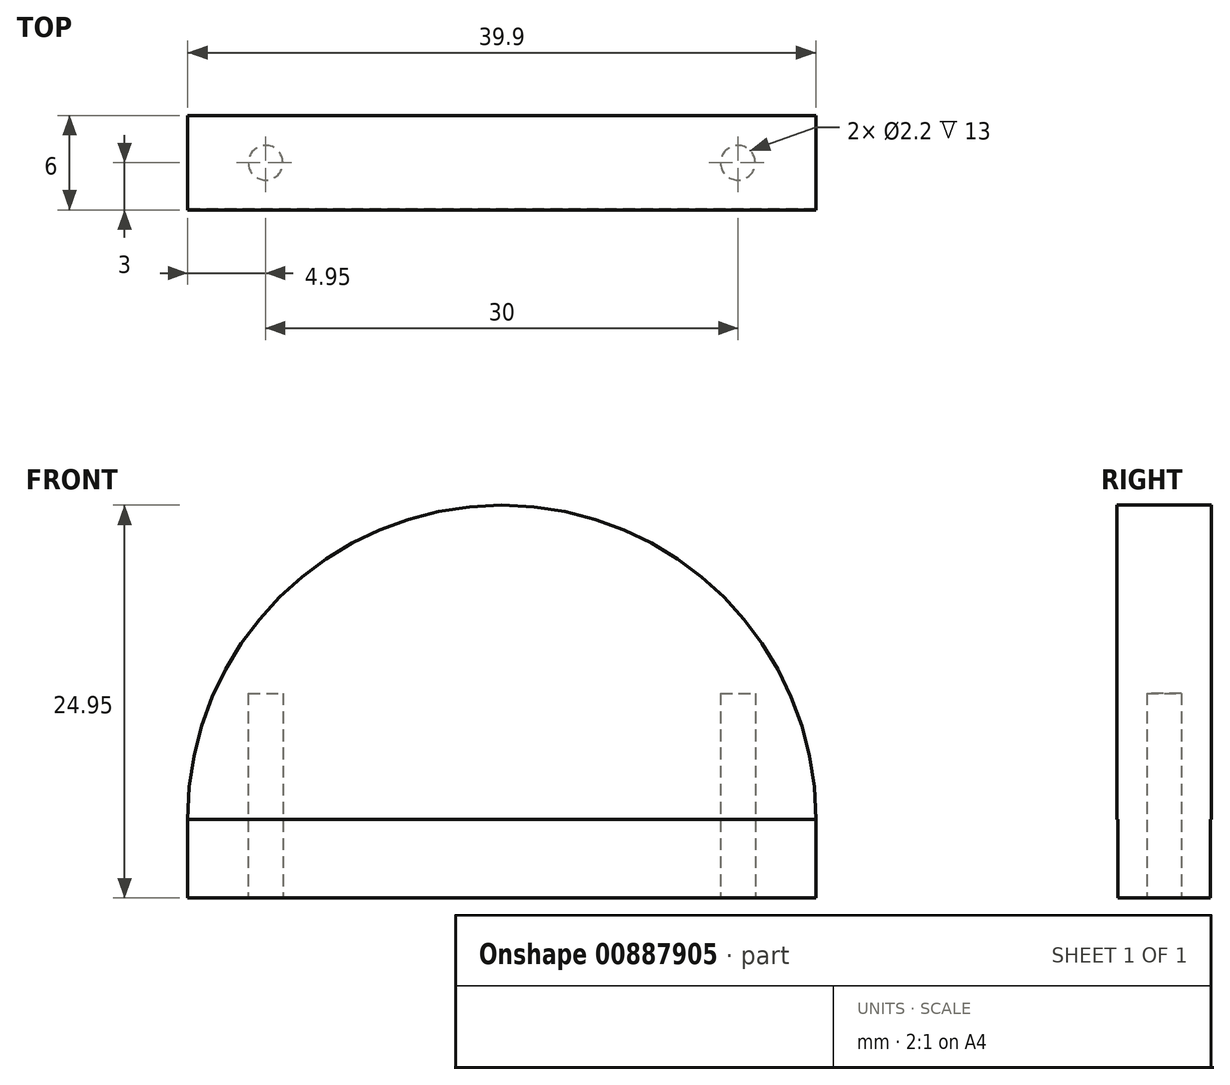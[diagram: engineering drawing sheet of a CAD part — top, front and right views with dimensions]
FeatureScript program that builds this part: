
annotation { "Feature Type Name" : "Feature", "Feature Type Description" : "" }
export const myFeature = defineFeature(function(context is Context, id is Id, definition is map)
    precondition{}
    {
        {
            var Q0;
            Q0=qCreatedBy(makeId("Top.planeOp"),FACE);
            var sketch = newSketch(context, id + "F0", { "sketchPlane" : qUnion([Q0])});
            skLineSegment(sketch, "E0.bottom", {"start": v(19.95, -2.95) * mm, "end": v(-19.95, -2.95) * mm});
            skLineSegment(sketch, "E0.top", {"start": v(19.95, 2.95) * mm, "end": v(-19.95, 2.95) * mm});
            skLineSegment(sketch, "E0.left", {"start": v(19.95, -2.95) * mm, "end": v(19.95, 2.95) * mm});
            skLineSegment(sketch, "E0.right", {"start": v(-19.95, -2.95) * mm, "end": v(-19.95, 2.95) * mm});
            skPoint(sketch, "E0.middle", {"position": v(0, 0) * mm});
            skSolve(sketch);
        }
        {
            var Q0;
            Q0=makeQuery(id+"F0.imprint","IMPRINT",FACE,{"disambiguationData":[TD([[makeQuery(id+"F0.imprint","IMPRINT",EDGE,{"derivedFrom":sQuery(id+"F0.wireOp",EDGE,"E0.bottom")}),-1.0]])]});
            extrude(context, id + "F1", {"entities" : qUnion([Q0]), "depth" : 5 * mm, "offsetDistance" : 25 * mm});
        }
        {
            var Q0;
            Q0=qCreatedBy(makeId("Front.planeOp"),FACE);
            var sketch = newSketch(context, id + "F2", { "sketchPlane" : qUnion([Q0])});
            skArc(sketch, "E1", {"start": v(19.95, 5) * mm, "mid": v(0, 24.95) * mm, "end": v(-19.95, 5) * mm});
            skLineSegment(sketch, "E2", {"start": v(-19.95, 5) * mm, "end": v(19.95, 5) * mm});
            skPoint(sketch, "E3.orphan", {"position": v(-19.31, 0) * mm});
            skSolve(sketch);
        }
        {
            var Q0;
            Q0 = qSketchRegion(id + "F2", true);
            extrude(context, id + "F3", {"entities" : qUnion([Q0]), "operationType" : NewBodyOperationType.ADD, "endBound" : BoundingType.SYMMETRIC, "depth" : 6 * mm, "offsetDistance" : 25 * mm});
        }
        {
            var Q0;
            Q0=makeQuery(id+"F1.opExtrude","CAP_FACE",FACE,{"disambiguationData":[OSD([sQuery(id+"F0.wireOp",EDGE,"E0.bottom"),sQuery(id+"F0.wireOp",EDGE,"E0.top"),sQuery(id+"F0.wireOp",EDGE,"E0.left"),sQuery(id+"F0.wireOp",EDGE,"E0.right")])],"isStart":true});
            var sketch = newSketch(context, id + "F4", { "sketchPlane" : qUnion([Q0])});
            skCircle(sketch, "E4", {"center": v(15, 0) * mm, "radius": 1.1 * mm});
            skCircle(sketch, "E5.MirrorC", {"center": v(-15, 0) * mm, "radius": 1.1 * mm});
            skSolve(sketch);
        }
        {
            var Q0;
            Q0 = qSketchRegion(id + "F4", true);
            extrude(context, id + "F5", {"entities" : qUnion([Q0]), "operationType" : NewBodyOperationType.REMOVE, "oppositeDirection" : true, "depth" : 13 * mm, "offsetDistance" : 25 * mm});
        }
    });
